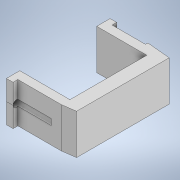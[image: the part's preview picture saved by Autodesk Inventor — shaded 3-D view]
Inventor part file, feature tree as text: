
AUTODESK INVENTOR PART (.ipt)
format: ipt  version: 2021 (Build 250183000, 183)  size: 160,256 bytes
history: native  units: mm
features: extrude x4, sketch x4, other x1
ambient origin geometry x8: Origin, YZ Plane, XZ Plane, XY Plane, X Axis, Y Axis, Z Axis, Center Point
bodies: Body1 (feature_tree)
feature tree (9):
  other  "Sólido1"
  extrude  "Extrusión1"  Depth=1.0mm
  extrude  "Extrusión2"  Depth=15.0mm
  extrude  "Extrusión3"  Depth=19.0mm
  extrude  "Extrusión4"  Depth=12.0mm
  sketch  "Boceto1"  dims[d0=22.0mm d1=1.0mm]
  sketch  "Boceto2"  dims[d2=15.0mm d3=15.0mm]
  sketch  "Boceto3"  dims[d4=4.0mm d5=19.0mm]
  sketch  "Boceto4"  dims[d6=4.0mm d7=5.0mm d8=5.0mm d9=12.0mm d10=0.0mm d11=1.0mm d12=1.0mm d13=12.0mm d14=0.0mm d15=2.0mm d16=2.0mm d17=12.0mm d18=0.0mm d19=12.0mm d20=0.0mm]
